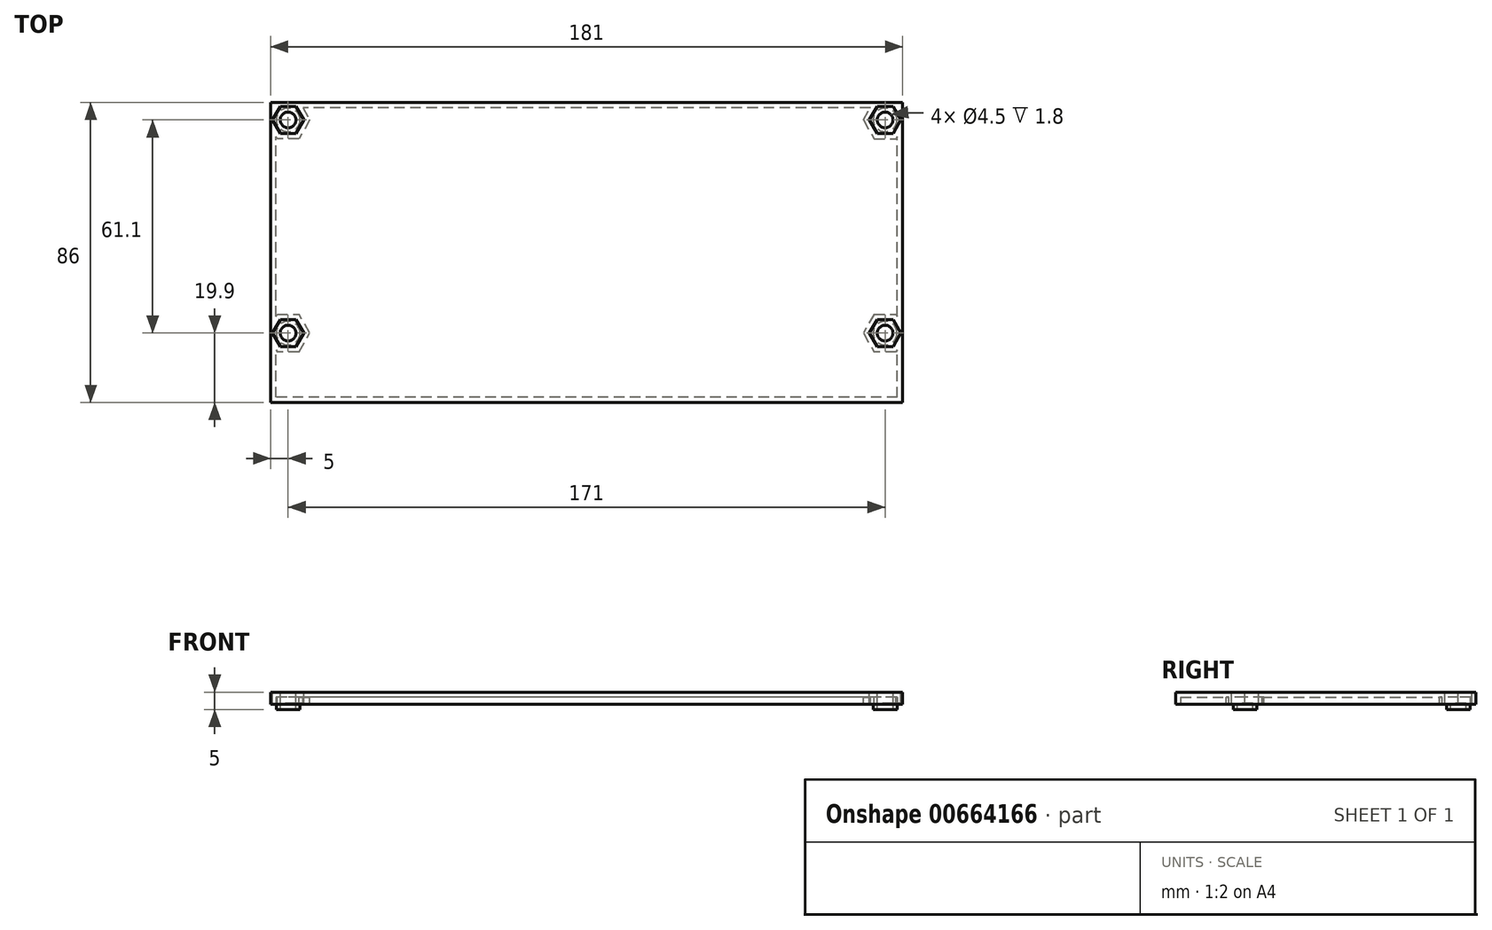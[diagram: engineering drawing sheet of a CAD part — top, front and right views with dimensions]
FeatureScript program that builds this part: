
annotation { "Feature Type Name" : "Feature", "Feature Type Description" : "" }
export const myFeature = defineFeature(function(context is Context, id is Id, definition is map)
    precondition{}
    {
        {
            var Q0;
            Q0=qCreatedBy(makeId("Top.planeOp"),FACE);
            var sketch = newSketch(context, id + "F0", { "sketchPlane" : qUnion([Q0])});
            skLineSegment(sketch, "E0.bottom", {"start": v(90.5, -43) * mm, "end": v(-90.5, -43) * mm});
            skLineSegment(sketch, "E0.top", {"start": v(90.5, 43) * mm, "end": v(-90.5, 43) * mm});
            skLineSegment(sketch, "E0.left", {"start": v(90.5, -43) * mm, "end": v(90.5, 43) * mm});
            skLineSegment(sketch, "E0.right", {"start": v(-90.5, -43) * mm, "end": v(-90.5, 43) * mm});
            skPoint(sketch, "E0.middle", {"position": v(0, 0) * mm});
            skSolve(sketch);
        }
        {
            var Q0;
            Q0=makeQuery(id+"F0.imprint","IMPRINT",FACE,{"disambiguationData":[TD([[makeQuery(id+"F0.imprint","IMPRINT",EDGE,{"derivedFrom":sQuery(id+"F0.wireOp",EDGE,"E0.bottom")}),-1.0]])]});
            extrude(context, id + "F1", {"entities" : qUnion([Q0]), "depth" : 3.5 * mm, "offsetDistance" : 25 * mm});
        }
        {
            var Q0;
            Q0=makeQuery(id+"F1.opExtrude","CAP_FACE",FACE,{"disambiguationData":[OSD([sQuery(id+"F0.wireOp",EDGE,"E0.bottom"),sQuery(id+"F0.wireOp",EDGE,"E0.top"),sQuery(id+"F0.wireOp",EDGE,"E0.left"),sQuery(id+"F0.wireOp",EDGE,"E0.right")])],"isStart":false});
            var sketch = newSketch(context, id + "F2", { "sketchPlane" : qUnion([Q0])});
            skCircle(sketch, "E1.cCircle", {"center": v(-85.5, 38) * mm, "radius": 3.9 * mm, "construction": true});
            skLineSegment(sketch, "E1.0", {"start": v(-83.25, 34.1) * mm, "end": v(-87.75, 34.1) * mm});
            skLineSegment(sketch, "E1.1", {"start": v(-87.75, 34.1) * mm, "end": v(-90, 38) * mm});
            skLineSegment(sketch, "E1.2", {"start": v(-90, 38) * mm, "end": v(-87.75, 41.9) * mm});
            skLineSegment(sketch, "E1.3", {"start": v(-87.75, 41.9) * mm, "end": v(-83.25, 41.9) * mm});
            skLineSegment(sketch, "E1.4", {"start": v(-83.25, 41.9) * mm, "end": v(-81, 38) * mm});
            skLineSegment(sketch, "E1.5", {"start": v(-81, 38) * mm, "end": v(-83.25, 34.1) * mm});
            skPoint(sketch, "E1.0.midPoint", {"position": v(-85.5, 34.1) * mm});
            skCircle(sketch, "E2", {"center": v(-85.5, 38) * mm, "radius": 2.25 * mm});
            skCircle(sketch, "E3", {"center": v(-85.5, 38) * mm, "radius": 3.4 * mm});
            skPoint(sketch, "E4.MirrorP", {"position": v(-85.5, -34.1) * mm});
            skLineSegment(sketch, "E5.0.1.0", {"start": v(-87.75, -19.2) * mm, "end": v(-83.25, -19.2) * mm});
            skCircle(sketch, "E5.0.1.1", {"center": v(-85.5, -23.1) * mm, "radius": 3.9 * mm, "construction": true});
            skCircle(sketch, "E5.0.1.2", {"center": v(-85.5, -23.1) * mm, "radius": 2.25 * mm});
            skCircle(sketch, "E5.0.1.3", {"center": v(-85.5, -23.1) * mm, "radius": 3.4 * mm});
            skLineSegment(sketch, "E5.0.1.4", {"start": v(-83.25, -19.2) * mm, "end": v(-81, -23.1) * mm});
            skLineSegment(sketch, "E5.0.1.5", {"start": v(-87.75, -27) * mm, "end": v(-90, -23.1) * mm});
            skLineSegment(sketch, "E5.0.1.6", {"start": v(-90, -23.1) * mm, "end": v(-87.75, -19.2) * mm});
            skLineSegment(sketch, "E5.0.1.7", {"start": v(-81, -23.1) * mm, "end": v(-83.25, -27) * mm});
            skPoint(sketch, "E5.0.1.8", {"position": v(-85.5, -27) * mm});
            skLineSegment(sketch, "E5.0.1.9", {"start": v(-83.25, -27) * mm, "end": v(-87.75, -27) * mm});
            skLineSegment(sketch, "E5.1.0.0", {"start": v(83.25, 41.9) * mm, "end": v(87.75, 41.9) * mm});
            skCircle(sketch, "E5.1.0.1", {"center": v(85.5, 38) * mm, "radius": 3.9 * mm, "construction": true});
            skCircle(sketch, "E5.1.0.2", {"center": v(85.5, 38) * mm, "radius": 2.25 * mm});
            skCircle(sketch, "E5.1.0.3", {"center": v(85.5, 38) * mm, "radius": 3.4 * mm});
            skLineSegment(sketch, "E5.1.0.4", {"start": v(87.75, 41.9) * mm, "end": v(90, 38) * mm});
            skLineSegment(sketch, "E5.1.0.5", {"start": v(83.25, 34.1) * mm, "end": v(81, 38) * mm});
            skLineSegment(sketch, "E5.1.0.6", {"start": v(81, 38) * mm, "end": v(83.25, 41.9) * mm});
            skLineSegment(sketch, "E5.1.0.7", {"start": v(90, 38) * mm, "end": v(87.75, 34.1) * mm});
            skPoint(sketch, "E5.1.0.8", {"position": v(85.5, 34.1) * mm});
            skLineSegment(sketch, "E5.1.0.9", {"start": v(87.75, 34.1) * mm, "end": v(83.25, 34.1) * mm});
            skLineSegment(sketch, "E5.1.1.0", {"start": v(83.25, -19.2) * mm, "end": v(87.75, -19.2) * mm});
            skCircle(sketch, "E5.1.1.1", {"center": v(85.5, -23.1) * mm, "radius": 3.9 * mm, "construction": true});
            skCircle(sketch, "E5.1.1.2", {"center": v(85.5, -23.1) * mm, "radius": 2.25 * mm});
            skCircle(sketch, "E5.1.1.3", {"center": v(85.5, -23.1) * mm, "radius": 3.4 * mm});
            skLineSegment(sketch, "E5.1.1.4", {"start": v(87.75, -19.2) * mm, "end": v(90, -23.1) * mm});
            skLineSegment(sketch, "E5.1.1.5", {"start": v(83.25, -27) * mm, "end": v(81, -23.1) * mm});
            skLineSegment(sketch, "E5.1.1.6", {"start": v(81, -23.1) * mm, "end": v(83.25, -19.2) * mm});
            skLineSegment(sketch, "E5.1.1.7", {"start": v(90, -23.1) * mm, "end": v(87.75, -27) * mm});
            skPoint(sketch, "E5.1.1.8", {"position": v(85.5, -27) * mm});
            skLineSegment(sketch, "E5.1.1.9", {"start": v(87.75, -27) * mm, "end": v(83.25, -27) * mm});
            skLineSegment(sketch, "E5.direction1", {"start": v(-87.75, 34.1) * mm, "end": v(83.25, 34.1) * mm, "construction": true});
            skLineSegment(sketch, "E5.direction2", {"start": v(-87.75, 34.1) * mm, "end": v(-87.75, -27) * mm, "construction": true});
            skSolve(sketch);
        }
        {
            var Q0;
            Q0=makeQuery(id+"F2.imprint","IMPRINT",FACE,{"disambiguationData":[TD([[makeQuery(id+"F2.imprint","IMPRINT",EDGE,{"derivedFrom":sQuery(id+"F2.wireOp",EDGE,"E2")}),-1.0]])]});
            var Q1;
            Q1=makeQuery(id+"F2.imprint","IMPRINT",FACE,{"disambiguationData":[TD([[makeQuery(id+"F2.imprint","IMPRINT",EDGE,{"derivedFrom":sQuery(id+"F2.wireOp",EDGE,"ab320155-eade-4191-b358-ac114a3cc9e52.MirrorC")}),1.0]])]});
            var Q2;
            Q2=makeQuery(id+"F2.imprint","IMPRINT",FACE,{"disambiguationData":[TD([[makeQuery(id+"F2.imprint","IMPRINT",EDGE,{"derivedFrom":sQuery(id+"F2.wireOp",EDGE,"a1412ccb-c3d3-4a4c-8767-e4c69d382a026.MirrorC")}),-1.0]])]});
            var Q3;
            Q3=makeQuery(id+"F2.imprint","IMPRINT",FACE,{"disambiguationData":[TD([[makeQuery(id+"F2.imprint","IMPRINT",EDGE,{"derivedFrom":sQuery(id+"F2.wireOp",EDGE,"7b19ad14-5b47-47b8-adc5-f563f86e351910.MirrorC")}),-1.0]])]});
            var Q4;
            Q4=makeQuery(id+"F2.imprint","IMPRINT",FACE,{"disambiguationData":[TD([[makeQuery(id+"F2.imprint","IMPRINT",EDGE,{"derivedFrom":sQuery(id+"F2.wireOp",EDGE,"E5.0.1.2")}),-1.0]])]});
            var Q5;
            Q5=makeQuery(id+"F2.imprint","IMPRINT",FACE,{"disambiguationData":[TD([[makeQuery(id+"F2.imprint","IMPRINT",EDGE,{"derivedFrom":sQuery(id+"F2.wireOp",EDGE,"E5.1.0.2")}),-1.0]])]});
            var Q6;
            Q6=makeQuery(id+"F2.imprint","IMPRINT",FACE,{"disambiguationData":[TD([[makeQuery(id+"F2.imprint","IMPRINT",EDGE,{"derivedFrom":sQuery(id+"F2.wireOp",EDGE,"E5.1.1.2")}),-1.0]])]});
            extrude(context, id + "F3", {"entities" : qUnion([Q0, Q1, Q2, Q3, Q4, Q5, Q6]), "operationType" : NewBodyOperationType.ADD, "oppositeDirection" : true, "depth" : 5 * mm, "offsetDistance" : 25 * mm});
        }
        {
            var Q0;
            Q0=makeQuery(id+"F2.imprint","IMPRINT",FACE,{"disambiguationData":[TD([[makeQuery(id+"F2.imprint","IMPRINT",EDGE,{"derivedFrom":sQuery(id+"F2.wireOp",EDGE,"E2")}),1.0]])]});
            var Q1;
            Q1=makeQuery(id+"F2.imprint","IMPRINT",FACE,{"disambiguationData":[TD([[makeQuery(id+"F2.imprint","IMPRINT",EDGE,{"derivedFrom":sQuery(id+"F2.wireOp",EDGE,"7b19ad14-5b47-47b8-adc5-f563f86e351910.MirrorC")}),1.0]])]});
            var Q2;
            Q2=makeQuery(id+"F2.imprint","IMPRINT",FACE,{"disambiguationData":[TD([[makeQuery(id+"F2.imprint","IMPRINT",EDGE,{"derivedFrom":sQuery(id+"F2.wireOp",EDGE,"ab320155-eade-4191-b358-ac114a3cc9e52.MirrorC")}),-1.0]])]});
            var Q3;
            Q3=makeQuery(id+"F2.imprint","IMPRINT",FACE,{"disambiguationData":[TD([[makeQuery(id+"F2.imprint","IMPRINT",EDGE,{"derivedFrom":sQuery(id+"F2.wireOp",EDGE,"a1412ccb-c3d3-4a4c-8767-e4c69d382a029.MirrorC")}),-1.0]])]});
            var Q4;
            Q4=makeQuery(id+"F2.imprint","IMPRINT",FACE,{"disambiguationData":[TD([[makeQuery(id+"F2.imprint","IMPRINT",EDGE,{"derivedFrom":sQuery(id+"F2.wireOp",EDGE,"E5.0.1.2")}),1.0]])]});
            var Q5;
            Q5=makeQuery(id+"F2.imprint","IMPRINT",FACE,{"disambiguationData":[TD([[makeQuery(id+"F2.imprint","IMPRINT",EDGE,{"derivedFrom":sQuery(id+"F2.wireOp",EDGE,"E5.1.1.2")}),1.0]])]});
            var Q6;
            Q6=makeQuery(id+"F2.imprint","IMPRINT",FACE,{"disambiguationData":[TD([[makeQuery(id+"F2.imprint","IMPRINT",EDGE,{"derivedFrom":sQuery(id+"F2.wireOp",EDGE,"E5.1.0.2")}),1.0]])]});
            extrude(context, id + "F4", {"entities" : qUnion([Q0, Q1, Q2, Q3, Q4, Q5, Q6]), "operationType" : NewBodyOperationType.REMOVE, "endBound" : BoundingType.THROUGH_ALL, "oppositeDirection" : true, "depth" : 25 * mm, "offsetDistance" : 25 * mm});
        }
        {
            var Q0;
            Q0 = qSketchRegion(id + "F2", true);
            var Q1;
            Q1=makeQuery(id+"F2.imprint","IMPRINT",FACE,{"disambiguationData":[TD([[makeQuery(id+"F2.imprint","IMPRINT",EDGE,{"derivedFrom":sQuery(id+"F2.wireOp",EDGE,"E2")}),-1.0]])]});
            var Q2;
            Q2=makeQuery(id+"F2.imprint","IMPRINT",FACE,{"disambiguationData":[TD([[makeQuery(id+"F2.imprint","IMPRINT",EDGE,{"derivedFrom":sQuery(id+"F2.wireOp",EDGE,"ab320155-eade-4191-b358-ac114a3cc9e52.MirrorC")}),1.0]])]});
            var Q3;
            Q3=makeQuery(id+"F2.imprint","IMPRINT",FACE,{"disambiguationData":[TD([[makeQuery(id+"F2.imprint","IMPRINT",EDGE,{"derivedFrom":sQuery(id+"F2.wireOp",EDGE,"a1412ccb-c3d3-4a4c-8767-e4c69d382a026.MirrorC")}),-1.0]])]});
            var Q4;
            Q4=makeQuery(id+"F2.imprint","IMPRINT",FACE,{"disambiguationData":[TD([[makeQuery(id+"F2.imprint","IMPRINT",EDGE,{"derivedFrom":sQuery(id+"F2.wireOp",EDGE,"7b19ad14-5b47-47b8-adc5-f563f86e351910.MirrorC")}),-1.0]])]});
            var Q5;
            Q5=makeQuery(id+"F2.imprint","IMPRINT",FACE,{"disambiguationData":[TD([[makeQuery(id+"F2.imprint","IMPRINT",EDGE,{"derivedFrom":sQuery(id+"F2.wireOp",EDGE,"E5.1.0.2")}),-1.0]])]});
            var Q6;
            Q6=makeQuery(id+"F2.imprint","IMPRINT",FACE,{"disambiguationData":[TD([[makeQuery(id+"F2.imprint","IMPRINT",EDGE,{"derivedFrom":sQuery(id+"F2.wireOp",EDGE,"E5.1.1.2")}),-1.0]])]});
            var Q7;
            Q7=makeQuery(id+"F2.imprint","IMPRINT",FACE,{"disambiguationData":[TD([[makeQuery(id+"F2.imprint","IMPRINT",EDGE,{"derivedFrom":sQuery(id+"F2.wireOp",EDGE,"E5.0.1.2")}),-1.0]])]});
            extrude(context, id + "F5", {"entities" : qUnion([Q0, Q1, Q2, Q3, Q4, Q5, Q6, Q7]), "operationType" : NewBodyOperationType.REMOVE, "oppositeDirection" : true, "depth" : 3.2 * mm, "offsetDistance" : 25 * mm});
        }
        {
            var Q0;
            {var subQ0=sQuery(id+"F0.wireOp",EDGE,"E0.left");var subQ1=sQuery(id+"F0.wireOp",EDGE,"E0.top");var subQ2=sQuery(id+"F0.wireOp",EDGE,"E0.right");var subQ3=sQuery(id+"F0.wireOp",EDGE,"E0.bottom");Q0=makeQuery(id+"F3.boolean.opBoolean","SPLIT",FACE,{"disambiguationData":[TD([makeQuery(id+"F1.opExtrude","SWEPT_FACE",FACE,{"disambiguationData":[OSD([subQ3])]})])],"derivedFrom":makeQuery(id+"F1.opExtrude","CAP_FACE",FACE,{"disambiguationData":[OSD([subQ3,subQ1,subQ0,subQ2])],"isStart":true})});}
            shell(context, id + "F6", {"entities" : qUnion([Q0]), "thickness" : 1.5 * mm});
        }
    });
